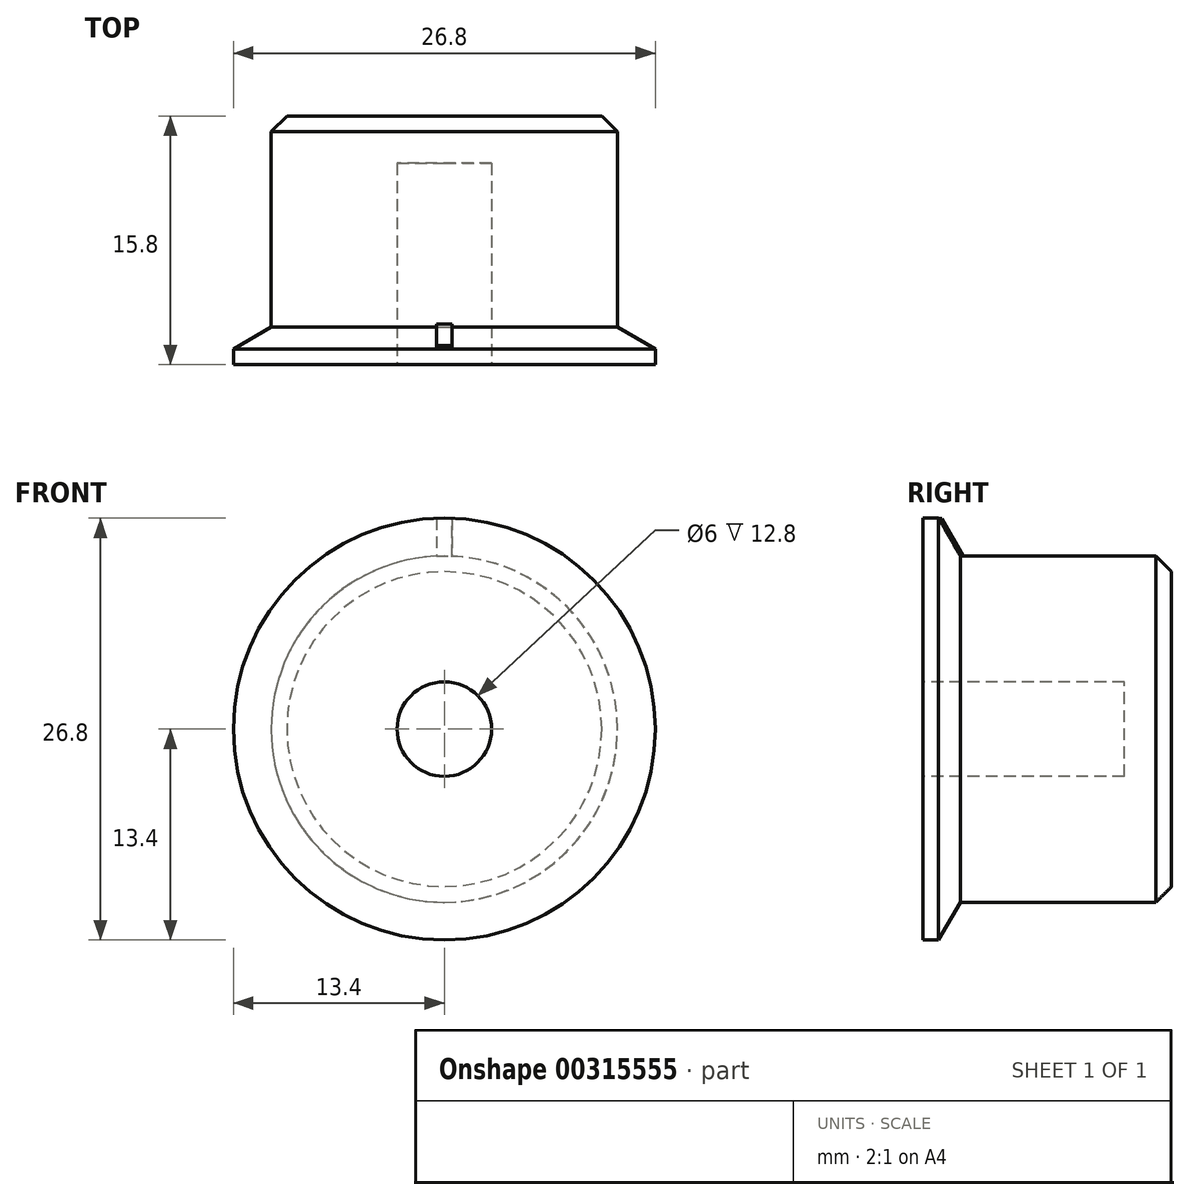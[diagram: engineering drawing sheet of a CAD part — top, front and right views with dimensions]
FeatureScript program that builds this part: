
annotation { "Feature Type Name" : "Feature", "Feature Type Description" : "" }
export const myFeature = defineFeature(function(context is Context, id is Id, definition is map)
    precondition{}
    {
        {
            var Q0;
            Q0=qCreatedBy(makeId("Top.planeOp"),FACE);
            var sketch = newSketch(context, id + "F0", { "sketchPlane" : qUnion([Q0])});
            skLineSegment(sketch, "E0", {"start": v(0, 15.8) * mm, "end": v(-11, 15.8) * mm});
            skLineSegment(sketch, "E1", {"start": v(-11, 15.8) * mm, "end": v(-11, 2.39) * mm});
            skLineSegment(sketch, "E2", {"start": v(-11, 2.39) * mm, "end": v(-13.4, 1) * mm});
            skLineSegment(sketch, "E3", {"start": v(-13.4, 1) * mm, "end": v(-13.4, 0) * mm});
            skLineSegment(sketch, "E4", {"start": v(-13.4, 0) * mm, "end": v(-3, 0) * mm});
            skLineSegment(sketch, "E5", {"start": v(-3, 0) * mm, "end": v(-3, 12.8) * mm});
            skLineSegment(sketch, "E6", {"start": v(-3, 12.8) * mm, "end": v(0, 12.8) * mm});
            skLineSegment(sketch, "E7", {"start": v(0, 12.8) * mm, "end": v(0, 15.8) * mm});
            skLineSegment(sketch, "E8", {"start": v(0, 0) * mm, "end": v(0, 28.18) * mm, "construction": true});
            skSolve(sketch);
        }
        {
            var Q0;
            Q0 = qSketchRegion(id + "F0", true);
            var Q1;
            Q1=sQuery(id+"F0.wireOp",EDGE,"E8");
            revolve(context, id + "F1", {"entities" : qUnion([Q0]), "axis" : qUnion([Q1]), "revolveType" : RevolveType.FULL});
        }
        {
            var Q0;
            Q0=makeQuery(id+"F1.opRevolve","SWEPT_FACE",FACE,{"disambiguationData":[OSD([sQuery(id+"F0.wireOp",EDGE,"E4")])]});
            var sketch = newSketch(context, id + "F2", { "sketchPlane" : qUnion([Q0])});
            skLineSegment(sketch, "E9.bottom", {"start": v(0.5, 13.4) * mm, "end": v(-0.5, 13.4) * mm});
            skLineSegment(sketch, "E9.top", {"start": v(0.5, 10.4) * mm, "end": v(-0.5, 10.4) * mm});
            skLineSegment(sketch, "E9.left", {"start": v(0.5, 13.4) * mm, "end": v(0.5, 10.4) * mm});
            skLineSegment(sketch, "E9.right", {"start": v(-0.5, 13.4) * mm, "end": v(-0.5, 10.4) * mm});
            skPoint(sketch, "E9.middle", {"position": v(0, 11.9) * mm});
            skSolve(sketch);
        }
        {
            var Q0;
            Q0 = qSketchRegion(id + "F2", true);
            extrude(context, id + "F3", {"entities" : qUnion([Q0]), "operationType" : NewBodyOperationType.ADD, "oppositeDirection" : true, "depth" : 3 * mm});
        }
        {
            var Q0;
            Q0=makeQuery(id+"F3.opExtrude","CAP_EDGE",EDGE,{"disambiguationData":[OSD([sQuery(id+"F2.wireOp",EDGE,"E9.bottom")])],"isStart":false});
            chamfer(context, id + "F4", {"entities" : qUnion([Q0]), "chamferType" : ChamferType.OFFSET_ANGLE, "width" : 1.8 * mm, "oppositeDirection" : false, "angle" : 60 * degree, "tangentPropagation" : true});
        }
        {
            var Q0;
            Q0=makeQuery(id+"F1.opRevolve","SWEPT_EDGE",EDGE,{"disambiguationData":[OSD([sQuery(id+"F0.wireOp",EDGE,"E0"),sQuery(id+"F0.wireOp",EDGE,"E1")])]});
            chamfer(context, id + "F5", {"entities" : qUnion([Q0]), "width" : 1 * mm, "tangentPropagation" : true});
        }
    });
